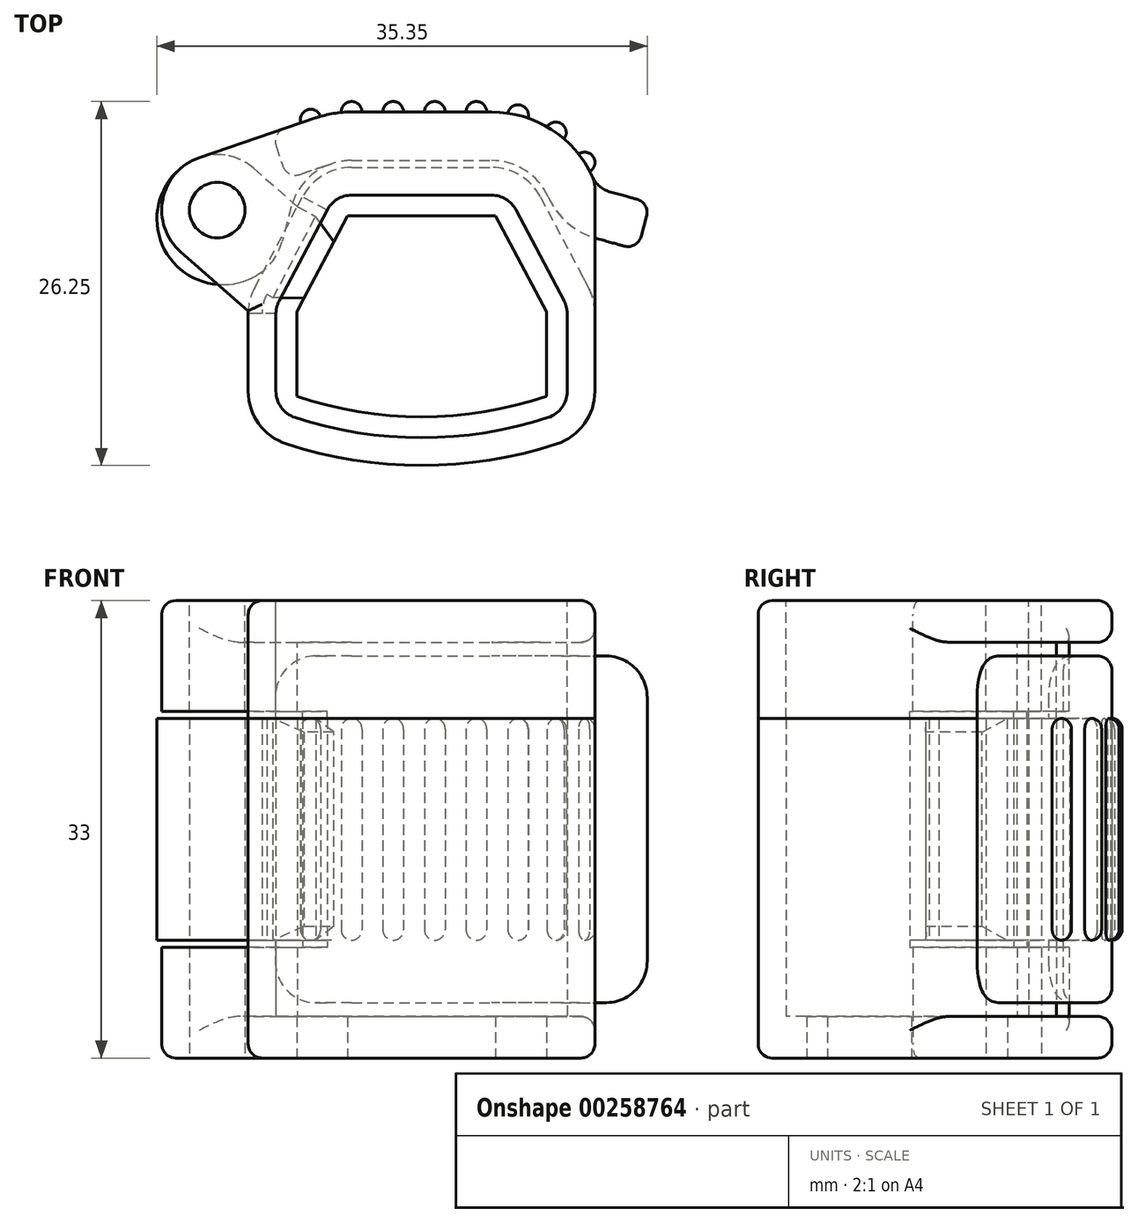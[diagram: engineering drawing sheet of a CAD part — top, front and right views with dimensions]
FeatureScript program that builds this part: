
annotation { "Feature Type Name" : "Feature", "Feature Type Description" : "" }
export const myFeature = defineFeature(function(context is Context, id is Id, definition is map)
    precondition{}
    {
        {
            var Q0;
            Q0=qCreatedBy(makeId("Top.planeOp"),FACE);
            var sketch = newSketch(context, id + "F0", { "sketchPlane" : qUnion([Q0])});
            skArc(sketch, "E0", {"start": v(-9.12, -27.9) * mm, "mid": v(0, -29.35) * mm, "end": v(9.12, -27.9) * mm});
            skLineSegment(sketch, "E1", {"start": v(-10.5, -26) * mm, "end": v(-10.5, -20.4) * mm});
            skLineSegment(sketch, "E2", {"start": v(-10.27, -19.47) * mm, "end": v(-6.81, -12.92) * mm});
            skLineSegment(sketch, "E3", {"start": v(-5.04, -11.85) * mm, "end": v(0, -11.85) * mm});
            skLineSegment(sketch, "E4", {"start": v(6.81, -12.92) * mm, "end": v(10.27, -19.47) * mm});
            skLineSegment(sketch, "E5", {"start": v(10.5, -20.4) * mm, "end": v(10.5, -26) * mm});
            skLineSegment(sketch, "E6", {"start": v(0, 0) * mm, "end": v(0, -29.35) * mm, "construction": true});
            skLineSegment(sketch, "E7", {"start": v(0, -11.85) * mm, "end": v(5.04, -11.85) * mm});
            skLineSegment(sketch, "E8", {"start": v(-6.25, -11.85) * mm, "end": v(0, 0) * mm, "construction": true});
            skLineSegment(sketch, "E9", {"start": v(6.25, -11.85) * mm, "end": v(0, 0) * mm, "construction": true});
            skPoint(sketch, "E10.visualSharp", {"position": v(-6.25, -11.85) * mm});
            skArc(sketch, "E10.filletArc", {"start": v(-5.04, -11.85) * mm, "mid": v(-6.08, -12.14) * mm, "end": v(-6.81, -12.92) * mm});
            skPoint(sketch, "E11.visualSharp", {"position": v(6.25, -11.85) * mm});
            skArc(sketch, "E11.filletArc", {"start": v(6.81, -12.92) * mm, "mid": v(6.08, -12.14) * mm, "end": v(5.04, -11.85) * mm});
            skPoint(sketch, "E12.visualSharp", {"position": v(10.5, -19.9) * mm});
            skArc(sketch, "E12.filletArc", {"start": v(10.5, -20.4) * mm, "mid": v(10.44, -19.92) * mm, "end": v(10.27, -19.47) * mm});
            skPoint(sketch, "E13.visualSharp", {"position": v(10.5, -27.4) * mm});
            skArc(sketch, "E13.filletArc", {"start": v(9.12, -27.9) * mm, "mid": v(10.12, -27.17) * mm, "end": v(10.5, -26) * mm});
            skPoint(sketch, "E14.visualSharp", {"position": v(-10.5, -27.4) * mm});
            skArc(sketch, "E14.filletArc", {"start": v(-10.5, -26) * mm, "mid": v(-10.12, -27.17) * mm, "end": v(-9.12, -27.9) * mm});
            skPoint(sketch, "E15.visualSharp", {"position": v(-10.5, -19.9) * mm});
            skArc(sketch, "E15.filletArc", {"start": v(-10.27, -19.47) * mm, "mid": v(-10.44, -19.92) * mm, "end": v(-10.5, -20.4) * mm});
            skSolve(sketch);
        }
        {
            var Q0;
            Q0=makeQuery(id+"F0.imprint","IMPRINT",FACE,{"disambiguationData":[TD([[makeQuery(id+"F0.imprint","IMPRINT",EDGE,{"derivedFrom":sQuery(id+"F0.wireOp",EDGE,"E0")}),1.0]])]});
            var sketch = newSketch(context, id + "F1", { "sketchPlane" : qUnion([Q0])});
            skLineSegment(sketch, "E16.0", {"start": v(-10.27, -19.47) * mm, "end": v(-7.19, -13.62) * mm, "construction": true});
            skLineSegment(sketch, "E17.0", {"start": v(6.81, -12.92) * mm, "end": v(10.27, -19.47) * mm});
            skLineSegment(sketch, "E18.0", {"start": v(0, -11.85) * mm, "end": v(5.04, -11.85) * mm});
            skLineSegment(sketch, "E19.0", {"start": v(-5.04, -11.85) * mm, "end": v(0, -11.85) * mm});
            skArc(sketch, "E20.0", {"start": v(-5.04, -11.85) * mm, "mid": v(-6.08, -12.14) * mm, "end": v(-6.81, -12.92) * mm});
            skArc(sketch, "E21.0", {"start": v(6.81, -12.92) * mm, "mid": v(6.08, -12.14) * mm, "end": v(5.04, -11.85) * mm});
            skLineSegment(sketch, "E22.0", {"start": v(-10.5, -26) * mm, "end": v(-10.5, -20.4) * mm});
            skArc(sketch, "E23.0", {"start": v(-10.5, -26) * mm, "mid": v(-10.12, -27.17) * mm, "end": v(-9.12, -27.9) * mm});
            skArc(sketch, "E24.0", {"start": v(-9.12, -27.9) * mm, "mid": v(0, -29.35) * mm, "end": v(9.12, -27.9) * mm});
            skArc(sketch, "E25.0", {"start": v(9.12, -27.9) * mm, "mid": v(10.12, -27.17) * mm, "end": v(10.5, -26) * mm});
            skLineSegment(sketch, "E26.0", {"start": v(10.5, -20.4) * mm, "end": v(10.5, -26) * mm});
            skArc(sketch, "E27.0", {"start": v(10.5, -20.4) * mm, "mid": v(10.44, -19.92) * mm, "end": v(10.27, -19.47) * mm});
            skArc(sketch, "E28.0", {"start": v(-10.27, -19.47) * mm, "mid": v(-10.44, -19.92) * mm, "end": v(-10.5, -20.4) * mm, "construction": true});
            skArc(sketch, "E29.0", {"start": v(-12.04, -18.54) * mm, "mid": v(-12.38, -19.44) * mm, "end": v(-12.5, -20.4) * mm});
            skLineSegment(sketch, "E29.1", {"start": v(-12.5, -26) * mm, "end": v(-12.5, -20.4) * mm});
            skArc(sketch, "E29.2", {"start": v(8.58, -11.98) * mm, "mid": v(7.1, -10.42) * mm, "end": v(5.04, -9.85) * mm});
            skLineSegment(sketch, "E29.3", {"start": v(0, -9.85) * mm, "end": v(5.04, -9.85) * mm});
            skLineSegment(sketch, "E29.4", {"start": v(-5.04, -9.85) * mm, "end": v(0, -9.85) * mm});
            skArc(sketch, "E29.5", {"start": v(-5.04, -9.85) * mm, "mid": v(-7.1, -10.42) * mm, "end": v(-8.58, -11.98) * mm});
            skLineSegment(sketch, "E29.6", {"start": v(8.58, -11.98) * mm, "end": v(12.04, -18.54) * mm});
            skArc(sketch, "E29.7", {"start": v(12.5, -20.4) * mm, "mid": v(12.38, -19.44) * mm, "end": v(12.04, -18.54) * mm});
            skLineSegment(sketch, "E29.8", {"start": v(-12.04, -18.54) * mm, "end": v(-8.95, -12.7) * mm});
            skLineSegment(sketch, "E29.9", {"start": v(12.5, -20.4) * mm, "end": v(12.5, -26) * mm});
            skArc(sketch, "E29.10", {"start": v(9.74, -29.8) * mm, "mid": v(11.74, -28.34) * mm, "end": v(12.5, -26) * mm});
            skArc(sketch, "E29.11", {"start": v(-9.74, -29.8) * mm, "mid": v(0, -31.35) * mm, "end": v(9.74, -29.8) * mm});
            skArc(sketch, "E29.12", {"start": v(-12.5, -26) * mm, "mid": v(-11.74, -28.34) * mm, "end": v(-9.74, -29.8) * mm});
            skArc(sketch, "E30.0", {"start": v(-11.15, -19) * mm, "mid": v(-11.41, -19.68) * mm, "end": v(-11.5, -20.4) * mm});
            skLineSegment(sketch, "E31", {"start": v(-10.5, -20.4) * mm, "end": v(-11.5, -20.4) * mm});
            skLineSegment(sketch, "E32", {"start": v(-11.15, -19) * mm, "end": v(-10.27, -19.47) * mm});
            skLineSegment(sketch, "E33", {"start": v(-6.81, -12.92) * mm, "end": v(-8.58, -11.98) * mm});
            skLineSegment(sketch, "E34.0", {"start": v(-7.19, -13.62) * mm, "end": v(-8.95, -12.7) * mm});
            skLineSegment(sketch, "E35", {"start": v(-7.19, -13.62) * mm, "end": v(-6.81, -12.92) * mm, "construction": true});
            skLineSegment(sketch, "E36", {"start": v(-11.15, -19) * mm, "end": v(-12.04, -18.54) * mm, "construction": true});
            skLineSegment(sketch, "E37", {"start": v(-11.5, -20.4) * mm, "end": v(-12.5, -20.4) * mm, "construction": true});
            skLineSegment(sketch, "E38.0", {"start": v(-8.94, -20.17) * mm, "end": v(-5.86, -14.32) * mm});
            skLineSegment(sketch, "E39", {"start": v(-7.19, -13.62) * mm, "end": v(-5.86, -14.32) * mm});
            skLineSegment(sketch, "E40", {"start": v(-10.27, -19.47) * mm, "end": v(-8.94, -20.17) * mm});
            skSolve(sketch);
        }
        {
            var Q0;
            Q0=makeQuery(id+"F0.imprint","IMPRINT",FACE,{"disambiguationData":[TD([[makeQuery(id+"F0.imprint","IMPRINT",EDGE,{"derivedFrom":sQuery(id+"F0.wireOp",EDGE,"E0")}),1.0]])]});
            var sketch = newSketch(context, id + "F2", { "sketchPlane" : qUnion([Q0])});
            skLineSegment(sketch, "E41.0", {"start": v(-10.27, -19.47) * mm, "end": v(-8.54, -16.2) * mm});
            skArc(sketch, "E42.0", {"start": v(-5.04, -11.85) * mm, "mid": v(-6.08, -12.14) * mm, "end": v(-6.81, -12.92) * mm});
            skLineSegment(sketch, "E43.0", {"start": v(-5.04, -11.85) * mm, "end": v(0, -11.85) * mm});
            skLineSegment(sketch, "E44.0", {"start": v(0, -11.85) * mm, "end": v(5.04, -11.85) * mm});
            skArc(sketch, "E45.0", {"start": v(6.81, -12.92) * mm, "mid": v(6.08, -12.14) * mm, "end": v(5.04, -11.85) * mm});
            skLineSegment(sketch, "E46.0", {"start": v(6.81, -12.92) * mm, "end": v(10.27, -19.47) * mm});
            skArc(sketch, "E47.0", {"start": v(10.5, -20.4) * mm, "mid": v(10.44, -19.92) * mm, "end": v(10.27, -19.47) * mm});
            skLineSegment(sketch, "E48.0", {"start": v(10.5, -20.4) * mm, "end": v(10.5, -26) * mm});
            skArc(sketch, "E49.0", {"start": v(9.12, -27.9) * mm, "mid": v(10.12, -27.17) * mm, "end": v(10.5, -26) * mm});
            skArc(sketch, "E50.0", {"start": v(-9.12, -27.9) * mm, "mid": v(0, -29.35) * mm, "end": v(9.12, -27.9) * mm});
            skArc(sketch, "E51.0", {"start": v(-10.5, -26) * mm, "mid": v(-10.12, -27.17) * mm, "end": v(-9.12, -27.9) * mm});
            skLineSegment(sketch, "E52.0", {"start": v(-10.5, -26) * mm, "end": v(-10.5, -20.4) * mm});
            skArc(sketch, "E53.0", {"start": v(-10.27, -19.47) * mm, "mid": v(-10.44, -19.92) * mm, "end": v(-10.5, -20.4) * mm});
            skArc(sketch, "E54.0", {"start": v(-5.04, -5.85) * mm, "mid": v(-6.35, -5.96) * mm, "end": v(-7.63, -6.28) * mm});
            skLineSegment(sketch, "E54.1", {"start": v(-5.04, -5.85) * mm, "end": v(0, -5.85) * mm});
            skLineSegment(sketch, "E54.2", {"start": v(0, -5.85) * mm, "end": v(5.04, -5.85) * mm});
            skArc(sketch, "E54.3", {"start": v(12.32, -10.52) * mm, "mid": v(9.37, -7.12) * mm, "end": v(5.04, -5.85) * mm});
            skLineSegment(sketch, "E55.0", {"start": v(-12.5, -26) * mm, "end": v(-12.5, -20.2) * mm});
            skLineSegment(sketch, "E55.1", {"start": v(12.5, -20.4) * mm, "end": v(12.5, -26) * mm});
            skArc(sketch, "E55.2", {"start": v(9.74, -29.8) * mm, "mid": v(11.74, -28.34) * mm, "end": v(12.5, -26) * mm});
            skArc(sketch, "E55.3", {"start": v(-9.74, -29.8) * mm, "mid": v(0, -31.35) * mm, "end": v(9.74, -29.8) * mm});
            skArc(sketch, "E55.4", {"start": v(-12.5, -26) * mm, "mid": v(-11.74, -28.34) * mm, "end": v(-9.74, -29.8) * mm});
            skLineSegment(sketch, "E56", {"start": v(12.5, -20.4) * mm, "end": v(12.5, -11.35) * mm});
            skPoint(sketch, "E57.visualSharp", {"position": v(12.5, -10.95) * mm});
            skArc(sketch, "E57.filletArc", {"start": v(12.5, -11.35) * mm, "mid": v(12.45, -10.93) * mm, "end": v(12.32, -10.52) * mm});
            skLineSegment(sketch, "E58", {"start": v(-8.54, -16.2) * mm, "end": v(-6.81, -12.92) * mm});
            skLineSegment(sketch, "E59", {"start": v(-8.54, -16.2) * mm, "end": v(-14.73, -12.93) * mm, "construction": true});
            skCircle(sketch, "E60", {"center": v(-14.73, -12.93) * mm, "radius": 2 * mm});
            skLineSegment(sketch, "E61", {"start": v(-16.02, -9.14) * mm, "end": v(-7.63, -6.28) * mm});
            skLineSegment(sketch, "E62", {"start": v(-17.37, -15.94) * mm, "end": v(-12.5, -20.2) * mm});
            skArc(sketch, "E63", {"start": v(-16.02, -9.14) * mm, "mid": v(-18.66, -12.15) * mm, "end": v(-17.37, -15.94) * mm});
            skArc(sketch, "E64", {"start": v(-17.37, -15.94) * mm, "mid": v(-10.8, -13.7) * mm, "end": v(-16.02, -9.14) * mm, "construction": true});
            skSolve(sketch);
        }
        {
            var Q0;
            Q0 = qSketchRegion(id + "F2", true);
            extrude(context, id + "F3", {"entities" : qUnion([Q0]), "depth" : 3 * mm});
        }
        {
            var Q0;
            Q0=makeQuery(id+"F3.opExtrude","CAP_FACE",FACE,{"disambiguationData":[OSD([sQuery(id+"F2.wireOp",EDGE,"E41.0"),sQuery(id+"F2.wireOp",EDGE,"E42.0"),sQuery(id+"F2.wireOp",EDGE,"E43.0"),sQuery(id+"F2.wireOp",EDGE,"E44.0"),sQuery(id+"F2.wireOp",EDGE,"E45.0"),sQuery(id+"F2.wireOp",EDGE,"E46.0"),sQuery(id+"F2.wireOp",EDGE,"E47.0"),sQuery(id+"F2.wireOp",EDGE,"E48.0"),sQuery(id+"F2.wireOp",EDGE,"E49.0"),sQuery(id+"F2.wireOp",EDGE,"E50.0"),sQuery(id+"F2.wireOp",EDGE,"E51.0"),sQuery(id+"F2.wireOp",EDGE,"E52.0"),sQuery(id+"F2.wireOp",EDGE,"E53.0"),sQuery(id+"F2.wireOp",EDGE,"E54.0"),sQuery(id+"F2.wireOp",EDGE,"E54.1"),sQuery(id+"F2.wireOp",EDGE,"E54.2"),sQuery(id+"F2.wireOp",EDGE,"E54.3"),sQuery(id+"F2.wireOp",EDGE,"E55.0"),sQuery(id+"F2.wireOp",EDGE,"E55.1"),sQuery(id+"F2.wireOp",EDGE,"E55.2"),sQuery(id+"F2.wireOp",EDGE,"E55.3"),sQuery(id+"F2.wireOp",EDGE,"E55.4"),sQuery(id+"F2.wireOp",EDGE,"E56"),sQuery(id+"F2.wireOp",EDGE,"E57.filletArc"),sQuery(id+"F2.wireOp",EDGE,"E58"),sQuery(id+"F2.wireOp",EDGE,"E60"),sQuery(id+"F2.wireOp",EDGE,"E61"),sQuery(id+"F2.wireOp",EDGE,"E62"),sQuery(id+"F2.wireOp",EDGE,"E63")])],"isStart":false});
            var sketch = newSketch(context, id + "F4", { "sketchPlane" : qUnion([Q0])});
            skLineSegment(sketch, "E65.0", {"start": v(-17.37, -15.94) * mm, "end": v(-17.37, -15.94) * mm});
            skCircle(sketch, "E66.0", {"center": v(-14.73, -12.93) * mm, "radius": 2 * mm});
            skArc(sketch, "E67.0", {"start": v(-16.02, -9.14) * mm, "mid": v(-18.66, -12.15) * mm, "end": v(-17.37, -15.94) * mm});
            skLineSegment(sketch, "E68.0", {"start": v(-17.37, -15.94) * mm, "end": v(-12.5, -20.2) * mm});
            skLineSegment(sketch, "E69.0", {"start": v(-12.5, -26) * mm, "end": v(-12.5, -20.2) * mm});
            skArc(sketch, "E70.0", {"start": v(-12.5, -26) * mm, "mid": v(-11.74, -28.34) * mm, "end": v(-9.74, -29.8) * mm});
            skArc(sketch, "E71.0", {"start": v(-9.74, -29.8) * mm, "mid": v(0, -31.35) * mm, "end": v(9.74, -29.8) * mm});
            skArc(sketch, "E72.0", {"start": v(9.74, -29.8) * mm, "mid": v(11.74, -28.34) * mm, "end": v(12.5, -26) * mm});
            skArc(sketch, "E73.0", {"start": v(9.12, -27.9) * mm, "mid": v(10.12, -27.17) * mm, "end": v(10.5, -26) * mm});
            skArc(sketch, "E74.0", {"start": v(-9.12, -27.9) * mm, "mid": v(0, -29.35) * mm, "end": v(9.12, -27.9) * mm});
            skArc(sketch, "E75.0", {"start": v(-10.5, -26) * mm, "mid": v(-10.12, -27.17) * mm, "end": v(-9.12, -27.9) * mm});
            skLineSegment(sketch, "E76.0", {"start": v(-10.5, -26) * mm, "end": v(-10.5, -20.4) * mm});
            skArc(sketch, "E77.0", {"start": v(-10.27, -19.47) * mm, "mid": v(-10.44, -19.92) * mm, "end": v(-10.5, -20.4) * mm});
            skLineSegment(sketch, "E78.0", {"start": v(-10.27, -19.47) * mm, "end": v(-8.54, -16.2) * mm});
            skLineSegment(sketch, "E79.0", {"start": v(-8.54, -16.2) * mm, "end": v(-6.81, -12.92) * mm});
            skArc(sketch, "E80.0", {"start": v(-5.04, -11.85) * mm, "mid": v(-6.08, -12.14) * mm, "end": v(-6.81, -12.92) * mm});
            skLineSegment(sketch, "E81.0", {"start": v(-5.04, -11.85) * mm, "end": v(0, -11.85) * mm});
            skLineSegment(sketch, "E82.0", {"start": v(0, -11.85) * mm, "end": v(5.04, -11.85) * mm});
            skArc(sketch, "E83.0", {"start": v(6.81, -12.92) * mm, "mid": v(6.08, -12.14) * mm, "end": v(5.04, -11.85) * mm});
            skLineSegment(sketch, "E84.0", {"start": v(6.81, -12.92) * mm, "end": v(10.27, -19.47) * mm});
            skArc(sketch, "E85.0", {"start": v(10.5, -20.4) * mm, "mid": v(10.44, -19.92) * mm, "end": v(10.27, -19.47) * mm});
            skLineSegment(sketch, "E86.0", {"start": v(10.5, -20.4) * mm, "end": v(10.5, -26) * mm});
            skLineSegment(sketch, "E87.0", {"start": v(12.5, -20.4) * mm, "end": v(12.5, -26) * mm});
            skArc(sketch, "E88.0", {"start": v(12.5, -20.4) * mm, "mid": v(12.38, -19.44) * mm, "end": v(12.04, -18.54) * mm});
            skLineSegment(sketch, "E89.0", {"start": v(8.58, -11.98) * mm, "end": v(12.04, -18.54) * mm});
            skArc(sketch, "E90.0", {"start": v(8.58, -11.98) * mm, "mid": v(7.1, -10.42) * mm, "end": v(5.04, -9.85) * mm});
            skLineSegment(sketch, "E91.0", {"start": v(0, -9.85) * mm, "end": v(5.04, -9.85) * mm});
            skLineSegment(sketch, "E92.0", {"start": v(-5.04, -9.85) * mm, "end": v(0, -9.85) * mm});
            skLineSegment(sketch, "E93.0", {"start": v(-8.54, -16.2) * mm, "end": v(-14.73, -12.93) * mm, "construction": true});
            skArc(sketch, "E94.0", {"start": v(-5.04, -9.85) * mm, "mid": v(-7.1, -10.42) * mm, "end": v(-8.58, -11.98) * mm});
            skLineSegment(sketch, "E95", {"start": v(-8.95, -12.67) * mm, "end": v(-8.58, -11.98) * mm});
            skLineSegment(sketch, "E96", {"start": v(-17.37, -15.94) * mm, "end": v(-12.78, -19.95) * mm});
            skArc(sketch, "E97", {"start": v(-17.37, -15.94) * mm, "mid": v(-11.72, -15.56) * mm, "end": v(-12.1, -9.92) * mm, "construction": true});
            skLineSegment(sketch, "E98", {"start": v(-12.1, -9.92) * mm, "end": v(-8.95, -12.67) * mm});
            skArc(sketch, "E99", {"start": v(-12.1, -9.92) * mm, "mid": v(-13.96, -9) * mm, "end": v(-16.02, -9.14) * mm});
            skLineSegment(sketch, "E100", {"start": v(-12.78, -19.95) * mm, "end": v(-8.95, -12.67) * mm, "construction": true});
            skSolve(sketch);
        }
        {
            var Q0;
            Q0 = qSketchRegion(id + "F4", true);
            extrude(context, id + "F5", {"entities" : qUnion([Q0]), "operationType" : NewBodyOperationType.ADD, "depth" : 5 * mm});
        }
        {
            var Q0;
            Q0=makeQuery(id+"F5.opExtrude","CAP_FACE",FACE,{"disambiguationData":[OSD([sQuery(id+"F4.wireOp",EDGE,"E66.0"),sQuery(id+"F4.wireOp",EDGE,"E67.0"),sQuery(id+"F4.wireOp",EDGE,"E68.0"),sQuery(id+"F4.wireOp",EDGE,"E69.0"),sQuery(id+"F4.wireOp",EDGE,"E70.0"),sQuery(id+"F4.wireOp",EDGE,"E71.0"),sQuery(id+"F4.wireOp",EDGE,"E72.0"),sQuery(id+"F4.wireOp",EDGE,"E73.0"),sQuery(id+"F4.wireOp",EDGE,"E74.0"),sQuery(id+"F4.wireOp",EDGE,"E75.0"),sQuery(id+"F4.wireOp",EDGE,"E76.0"),sQuery(id+"F4.wireOp",EDGE,"E77.0"),sQuery(id+"F4.wireOp",EDGE,"E78.0"),sQuery(id+"F4.wireOp",EDGE,"E79.0"),sQuery(id+"F4.wireOp",EDGE,"E80.0"),sQuery(id+"F4.wireOp",EDGE,"E81.0"),sQuery(id+"F4.wireOp",EDGE,"E82.0"),sQuery(id+"F4.wireOp",EDGE,"E83.0"),sQuery(id+"F4.wireOp",EDGE,"E84.0"),sQuery(id+"F4.wireOp",EDGE,"E85.0"),sQuery(id+"F4.wireOp",EDGE,"E86.0"),sQuery(id+"F4.wireOp",EDGE,"E87.0"),sQuery(id+"F4.wireOp",EDGE,"E88.0"),sQuery(id+"F4.wireOp",EDGE,"E89.0"),sQuery(id+"F4.wireOp",EDGE,"E90.0"),sQuery(id+"F4.wireOp",EDGE,"E91.0"),sQuery(id+"F4.wireOp",EDGE,"E92.0"),sQuery(id+"F4.wireOp",EDGE,"E94.0"),sQuery(id+"F4.wireOp",EDGE,"E95"),sQuery(id+"F4.wireOp",EDGE,"E96"),sQuery(id+"F4.wireOp",EDGE,"E98"),sQuery(id+"F4.wireOp",EDGE,"E99")])],"isStart":false});
            var sketch = newSketch(context, id + "F6", { "sketchPlane" : qUnion([Q0])});
            skLineSegment(sketch, "E101.0", {"start": v(-12.5, -26) * mm, "end": v(-12.5, -20.4) * mm});
            skLineSegment(sketch, "E102.0", {"start": v(-10.5, -26) * mm, "end": v(-10.5, -20.4) * mm});
            skArc(sketch, "E103.0", {"start": v(-10.5, -26) * mm, "mid": v(-10.12, -27.17) * mm, "end": v(-9.12, -27.9) * mm});
            skLineSegment(sketch, "E104.0", {"start": v(-10.5, -20.4) * mm, "end": v(-11.5, -20.4) * mm});
            skLineSegment(sketch, "E105.0", {"start": v(-11.5, -20.4) * mm, "end": v(-12.5, -20.4) * mm});
            skArc(sketch, "E106.0", {"start": v(-12.5, -26) * mm, "mid": v(-11.74, -28.34) * mm, "end": v(-9.74, -29.8) * mm});
            skArc(sketch, "E107.0", {"start": v(-9.74, -29.8) * mm, "mid": v(0, -31.35) * mm, "end": v(9.74, -29.8) * mm});
            skArc(sketch, "E108.0", {"start": v(-9.12, -27.9) * mm, "mid": v(0, -29.35) * mm, "end": v(9.12, -27.9) * mm});
            skArc(sketch, "E109.0", {"start": v(9.12, -27.9) * mm, "mid": v(10.12, -27.17) * mm, "end": v(10.5, -26) * mm});
            skArc(sketch, "E110.0", {"start": v(9.74, -29.8) * mm, "mid": v(11.74, -28.34) * mm, "end": v(12.5, -26) * mm});
            skLineSegment(sketch, "E111.0", {"start": v(12.5, -20.4) * mm, "end": v(12.5, -26) * mm});
            skLineSegment(sketch, "E112.0", {"start": v(10.5, -20.4) * mm, "end": v(10.5, -26) * mm});
            skArc(sketch, "E113.0", {"start": v(10.5, -20.4) * mm, "mid": v(10.44, -19.92) * mm, "end": v(10.27, -19.47) * mm});
            skArc(sketch, "E114.0", {"start": v(12.5, -20.4) * mm, "mid": v(12.38, -19.44) * mm, "end": v(12.04, -18.54) * mm});
            skLineSegment(sketch, "E115.0", {"start": v(8.58, -11.98) * mm, "end": v(12.04, -18.54) * mm});
            skLineSegment(sketch, "E116.0", {"start": v(6.81, -12.92) * mm, "end": v(10.27, -19.47) * mm});
            skArc(sketch, "E117.0", {"start": v(6.81, -12.92) * mm, "mid": v(6.08, -12.14) * mm, "end": v(5.04, -11.85) * mm});
            skArc(sketch, "E118.0", {"start": v(8.58, -11.98) * mm, "mid": v(7.1, -10.42) * mm, "end": v(5.04, -9.85) * mm});
            skLineSegment(sketch, "E119.0", {"start": v(0, -9.85) * mm, "end": v(5.04, -9.85) * mm});
            skLineSegment(sketch, "E120.0", {"start": v(0, -11.85) * mm, "end": v(5.04, -11.85) * mm});
            skLineSegment(sketch, "E121.0", {"start": v(-5.04, -9.85) * mm, "end": v(0, -9.85) * mm});
            skLineSegment(sketch, "E122.0", {"start": v(-5.04, -11.85) * mm, "end": v(0, -11.85) * mm});
            skArc(sketch, "E123.0", {"start": v(-5.04, -11.85) * mm, "mid": v(-6.08, -12.14) * mm, "end": v(-6.81, -12.92) * mm});
            skArc(sketch, "E124.0", {"start": v(-5.04, -9.85) * mm, "mid": v(-7.1, -10.42) * mm, "end": v(-8.58, -11.98) * mm});
            skLineSegment(sketch, "E125.0", {"start": v(-6.81, -12.92) * mm, "end": v(-8.58, -11.98) * mm});
            skSolve(sketch);
        }
        {
            var Q0;
            Q0 = qSketchRegion(id + "F6", true);
            extrude(context, id + "F7", {"entities" : qUnion([Q0]), "operationType" : NewBodyOperationType.ADD, "depth" : 0.5 * mm});
        }
        {
            var Q0;
            Q0=makeQuery(id+"F0.imprint","IMPRINT",FACE,{"disambiguationData":[TD([[makeQuery(id+"F0.imprint","IMPRINT",EDGE,{"derivedFrom":sQuery(id+"F0.wireOp",EDGE,"E0")}),1.0]])]});
            var sketch = newSketch(context, id + "F8", { "sketchPlane" : qUnion([Q0])});
            skLineSegment(sketch, "E126.0.0", {"start": v(-12.5, -20.2) * mm, "end": v(-12.5, -26) * mm});
            skArc(sketch, "E126.0.1", {"start": v(-12.5, -26) * mm, "mid": v(-11.74, -28.34) * mm, "end": v(-9.74, -29.8) * mm});
            skArc(sketch, "E126.0.2", {"start": v(-9.74, -29.8) * mm, "mid": v(0, -31.35) * mm, "end": v(9.74, -29.8) * mm});
            skArc(sketch, "E126.0.3", {"start": v(9.74, -29.8) * mm, "mid": v(11.74, -28.34) * mm, "end": v(12.5, -26) * mm});
            skLineSegment(sketch, "E126.0.4", {"start": v(12.5, -26) * mm, "end": v(12.5, -20.4) * mm});
            skLineSegment(sketch, "E126.0.5", {"start": v(12.5, -20.4) * mm, "end": v(12.5, -11.35) * mm});
            skArc(sketch, "E126.0.6", {"start": v(12.5, -11.35) * mm, "mid": v(12.45, -10.93) * mm, "end": v(12.32, -10.52) * mm});
            skArc(sketch, "E126.0.7", {"start": v(12.32, -10.52) * mm, "mid": v(9.37, -7.12) * mm, "end": v(5.04, -5.85) * mm});
            skLineSegment(sketch, "E126.0.8", {"start": v(5.04, -5.85) * mm, "end": v(0, -5.85) * mm});
            skLineSegment(sketch, "E126.0.9", {"start": v(0, -5.85) * mm, "end": v(-5.04, -5.85) * mm});
            skArc(sketch, "E126.0.10", {"start": v(-5.04, -5.85) * mm, "mid": v(-6.35, -5.96) * mm, "end": v(-7.63, -6.28) * mm});
            skLineSegment(sketch, "E126.0.11", {"start": v(-7.63, -6.28) * mm, "end": v(-16.02, -9.14) * mm});
            skArc(sketch, "E126.0.12", {"start": v(-16.02, -9.14) * mm, "mid": v(-18.66, -12.15) * mm, "end": v(-17.37, -15.94) * mm});
            skLineSegment(sketch, "E126.0.13", {"start": v(-17.37, -15.94) * mm, "end": v(-12.5, -20.2) * mm});
            skCircle(sketch, "E127.0", {"center": v(-14.73, -12.93) * mm, "radius": 2 * mm});
            skLineSegment(sketch, "E128.0.0", {"start": v(5.04, -11.85) * mm, "end": v(0, -11.85) * mm, "construction": true});
            skLineSegment(sketch, "E128.0.1", {"start": v(0, -11.85) * mm, "end": v(-5.04, -11.85) * mm, "construction": true});
            skArc(sketch, "E128.0.2", {"start": v(-5.04, -11.85) * mm, "mid": v(-6.08, -12.14) * mm, "end": v(-6.81, -12.92) * mm, "construction": true});
            skLineSegment(sketch, "E128.0.3", {"start": v(-6.81, -12.92) * mm, "end": v(-8.54, -16.2) * mm, "construction": true});
            skLineSegment(sketch, "E128.0.4", {"start": v(-8.54, -16.2) * mm, "end": v(-10.27, -19.47) * mm, "construction": true});
            skArc(sketch, "E128.0.5", {"start": v(-10.27, -19.47) * mm, "mid": v(-10.44, -19.92) * mm, "end": v(-10.5, -20.4) * mm, "construction": true});
            skLineSegment(sketch, "E128.0.6", {"start": v(-10.5, -20.4) * mm, "end": v(-10.5, -26) * mm, "construction": true});
            skArc(sketch, "E128.0.7", {"start": v(-10.5, -26) * mm, "mid": v(-10.12, -27.17) * mm, "end": v(-9.12, -27.9) * mm, "construction": true});
            skArc(sketch, "E128.0.8", {"start": v(-9.12, -27.9) * mm, "mid": v(0, -29.35) * mm, "end": v(9.12, -27.9) * mm, "construction": true});
            skArc(sketch, "E128.0.9", {"start": v(9.12, -27.9) * mm, "mid": v(10.12, -27.17) * mm, "end": v(10.5, -26) * mm, "construction": true});
            skLineSegment(sketch, "E128.0.10", {"start": v(10.5, -26) * mm, "end": v(10.5, -20.4) * mm, "construction": true});
            skArc(sketch, "E128.0.11", {"start": v(10.5, -20.4) * mm, "mid": v(10.44, -19.92) * mm, "end": v(10.27, -19.47) * mm, "construction": true});
            skLineSegment(sketch, "E128.0.12", {"start": v(10.27, -19.47) * mm, "end": v(6.81, -12.92) * mm, "construction": true});
            skArc(sketch, "E128.0.13", {"start": v(6.81, -12.92) * mm, "mid": v(6.08, -12.14) * mm, "end": v(5.04, -11.85) * mm, "construction": true});
            skLineSegment(sketch, "E129.0", {"start": v(9, -20.28) * mm, "end": v(5.35, -13.35) * mm});
            skLineSegment(sketch, "E129.1", {"start": v(9, -26.35) * mm, "end": v(9, -20.28) * mm});
            skLineSegment(sketch, "E129.2", {"start": v(5.35, -13.35) * mm, "end": v(0, -13.35) * mm});
            skArc(sketch, "E129.3", {"start": v(-9, -26.35) * mm, "mid": v(0, -27.85) * mm, "end": v(9, -26.35) * mm});
            skLineSegment(sketch, "E129.4", {"start": v(0, -13.35) * mm, "end": v(-5.35, -13.35) * mm});
            skLineSegment(sketch, "E129.5", {"start": v(-5.35, -13.35) * mm, "end": v(-7.21, -16.9) * mm});
            skLineSegment(sketch, "E129.6", {"start": v(-7.21, -16.9) * mm, "end": v(-9, -20.28) * mm});
            skLineSegment(sketch, "E129.7", {"start": v(-9, -20.28) * mm, "end": v(-9, -26.35) * mm});
            skSolve(sketch);
        }
        {
            var Q0;
            Q0=makeQuery(id+"F3.opExtrude","SWEPT_BODY",BODY,{"disambiguationData":[OSD([sQuery(id+"F2.wireOp",EDGE,"E41.0"),sQuery(id+"F2.wireOp",EDGE,"E42.0"),sQuery(id+"F2.wireOp",EDGE,"E43.0"),sQuery(id+"F2.wireOp",EDGE,"E44.0"),sQuery(id+"F2.wireOp",EDGE,"E45.0"),sQuery(id+"F2.wireOp",EDGE,"E46.0"),sQuery(id+"F2.wireOp",EDGE,"E47.0"),sQuery(id+"F2.wireOp",EDGE,"E48.0"),sQuery(id+"F2.wireOp",EDGE,"E49.0"),sQuery(id+"F2.wireOp",EDGE,"E50.0"),sQuery(id+"F2.wireOp",EDGE,"E51.0"),sQuery(id+"F2.wireOp",EDGE,"E52.0"),sQuery(id+"F2.wireOp",EDGE,"E53.0"),sQuery(id+"F2.wireOp",EDGE,"E54.0"),sQuery(id+"F2.wireOp",EDGE,"E54.1"),sQuery(id+"F2.wireOp",EDGE,"E54.2"),sQuery(id+"F2.wireOp",EDGE,"E54.3"),sQuery(id+"F2.wireOp",EDGE,"E55.0"),sQuery(id+"F2.wireOp",EDGE,"E55.1"),sQuery(id+"F2.wireOp",EDGE,"E55.2"),sQuery(id+"F2.wireOp",EDGE,"E55.3"),sQuery(id+"F2.wireOp",EDGE,"E55.4"),sQuery(id+"F2.wireOp",EDGE,"E56"),sQuery(id+"F2.wireOp",EDGE,"E57.filletArc"),sQuery(id+"F2.wireOp",EDGE,"E58"),sQuery(id+"F2.wireOp",EDGE,"E60"),sQuery(id+"F2.wireOp",EDGE,"E61"),sQuery(id+"F2.wireOp",EDGE,"E62"),sQuery(id+"F2.wireOp",EDGE,"E63")])]});
            var Q1;
            Q1=makeQuery(id+"F7.opExtrude","CAP_FACE",FACE,{"disambiguationData":[OSD([sQuery(id+"F6.wireOp",EDGE,"E101.0"),sQuery(id+"F6.wireOp",EDGE,"E102.0"),sQuery(id+"F6.wireOp",EDGE,"E103.0"),sQuery(id+"F6.wireOp",EDGE,"E104.0"),sQuery(id+"F6.wireOp",EDGE,"E105.0"),sQuery(id+"F6.wireOp",EDGE,"E106.0"),sQuery(id+"F6.wireOp",EDGE,"E107.0"),sQuery(id+"F6.wireOp",EDGE,"E108.0"),sQuery(id+"F6.wireOp",EDGE,"E109.0"),sQuery(id+"F6.wireOp",EDGE,"E110.0"),sQuery(id+"F6.wireOp",EDGE,"E111.0"),sQuery(id+"F6.wireOp",EDGE,"E112.0"),sQuery(id+"F6.wireOp",EDGE,"E113.0"),sQuery(id+"F6.wireOp",EDGE,"E114.0"),sQuery(id+"F6.wireOp",EDGE,"E115.0"),sQuery(id+"F6.wireOp",EDGE,"E116.0"),sQuery(id+"F6.wireOp",EDGE,"E117.0"),sQuery(id+"F6.wireOp",EDGE,"E118.0"),sQuery(id+"F6.wireOp",EDGE,"E119.0"),sQuery(id+"F6.wireOp",EDGE,"E120.0"),sQuery(id+"F6.wireOp",EDGE,"E121.0"),sQuery(id+"F6.wireOp",EDGE,"E122.0"),sQuery(id+"F6.wireOp",EDGE,"E123.0"),sQuery(id+"F6.wireOp",EDGE,"E124.0"),sQuery(id+"F6.wireOp",EDGE,"E125.0")])],"isStart":false});
            transform(context, id + "F9", {"entities" : qUnion([Q0]), "transformType" : TransformType.TRANSLATION_DISTANCE, "transformDirection" : qUnion([Q1]), "distance" : 33 * mm, "makeCopy" : false});
        }
        {
            var Q0;
            Q0=makeQuery(id+"F3.opExtrude","SWEPT_BODY",BODY,{"disambiguationData":[OSD([sQuery(id+"F2.wireOp",EDGE,"E41.0"),sQuery(id+"F2.wireOp",EDGE,"E42.0"),sQuery(id+"F2.wireOp",EDGE,"E43.0"),sQuery(id+"F2.wireOp",EDGE,"E44.0"),sQuery(id+"F2.wireOp",EDGE,"E45.0"),sQuery(id+"F2.wireOp",EDGE,"E46.0"),sQuery(id+"F2.wireOp",EDGE,"E47.0"),sQuery(id+"F2.wireOp",EDGE,"E48.0"),sQuery(id+"F2.wireOp",EDGE,"E49.0"),sQuery(id+"F2.wireOp",EDGE,"E50.0"),sQuery(id+"F2.wireOp",EDGE,"E51.0"),sQuery(id+"F2.wireOp",EDGE,"E52.0"),sQuery(id+"F2.wireOp",EDGE,"E53.0"),sQuery(id+"F2.wireOp",EDGE,"E54.0"),sQuery(id+"F2.wireOp",EDGE,"E54.1"),sQuery(id+"F2.wireOp",EDGE,"E54.2"),sQuery(id+"F2.wireOp",EDGE,"E54.3"),sQuery(id+"F2.wireOp",EDGE,"E55.0"),sQuery(id+"F2.wireOp",EDGE,"E55.1"),sQuery(id+"F2.wireOp",EDGE,"E55.2"),sQuery(id+"F2.wireOp",EDGE,"E55.3"),sQuery(id+"F2.wireOp",EDGE,"E55.4"),sQuery(id+"F2.wireOp",EDGE,"E56"),sQuery(id+"F2.wireOp",EDGE,"E57.filletArc"),sQuery(id+"F2.wireOp",EDGE,"E58"),sQuery(id+"F2.wireOp",EDGE,"E60"),sQuery(id+"F2.wireOp",EDGE,"E61"),sQuery(id+"F2.wireOp",EDGE,"E62"),sQuery(id+"F2.wireOp",EDGE,"E63")])]});
            var Q1;
            Q1=makeQuery(id+"F3.opExtrude","CAP_FACE",FACE,{"disambiguationData":[OSD([sQuery(id+"F2.wireOp",EDGE,"E41.0"),sQuery(id+"F2.wireOp",EDGE,"E42.0"),sQuery(id+"F2.wireOp",EDGE,"E43.0"),sQuery(id+"F2.wireOp",EDGE,"E44.0"),sQuery(id+"F2.wireOp",EDGE,"E45.0"),sQuery(id+"F2.wireOp",EDGE,"E46.0"),sQuery(id+"F2.wireOp",EDGE,"E47.0"),sQuery(id+"F2.wireOp",EDGE,"E48.0"),sQuery(id+"F2.wireOp",EDGE,"E49.0"),sQuery(id+"F2.wireOp",EDGE,"E50.0"),sQuery(id+"F2.wireOp",EDGE,"E51.0"),sQuery(id+"F2.wireOp",EDGE,"E52.0"),sQuery(id+"F2.wireOp",EDGE,"E53.0"),sQuery(id+"F2.wireOp",EDGE,"E54.0"),sQuery(id+"F2.wireOp",EDGE,"E54.1"),sQuery(id+"F2.wireOp",EDGE,"E54.2"),sQuery(id+"F2.wireOp",EDGE,"E54.3"),sQuery(id+"F2.wireOp",EDGE,"E55.0"),sQuery(id+"F2.wireOp",EDGE,"E55.1"),sQuery(id+"F2.wireOp",EDGE,"E55.2"),sQuery(id+"F2.wireOp",EDGE,"E55.3"),sQuery(id+"F2.wireOp",EDGE,"E55.4"),sQuery(id+"F2.wireOp",EDGE,"E56"),sQuery(id+"F2.wireOp",EDGE,"E57.filletArc"),sQuery(id+"F2.wireOp",EDGE,"E58"),sQuery(id+"F2.wireOp",EDGE,"E60"),sQuery(id+"F2.wireOp",EDGE,"E61"),sQuery(id+"F2.wireOp",EDGE,"E62"),sQuery(id+"F2.wireOp",EDGE,"E63")])],"isStart":true});
            mirror(context, id + "F10", {"entities" : qUnion([Q0]), "mirrorPlane" : qUnion([Q1])});
        }
        {
            var Q0;
            Q0=makeQuery(id+"F3.opExtrude","SWEPT_BODY",BODY,{"disambiguationData":[OSD([sQuery(id+"F2.wireOp",EDGE,"E41.0"),sQuery(id+"F2.wireOp",EDGE,"E42.0"),sQuery(id+"F2.wireOp",EDGE,"E43.0"),sQuery(id+"F2.wireOp",EDGE,"E44.0"),sQuery(id+"F2.wireOp",EDGE,"E45.0"),sQuery(id+"F2.wireOp",EDGE,"E46.0"),sQuery(id+"F2.wireOp",EDGE,"E47.0"),sQuery(id+"F2.wireOp",EDGE,"E48.0"),sQuery(id+"F2.wireOp",EDGE,"E49.0"),sQuery(id+"F2.wireOp",EDGE,"E50.0"),sQuery(id+"F2.wireOp",EDGE,"E51.0"),sQuery(id+"F2.wireOp",EDGE,"E52.0"),sQuery(id+"F2.wireOp",EDGE,"E53.0"),sQuery(id+"F2.wireOp",EDGE,"E54.0"),sQuery(id+"F2.wireOp",EDGE,"E54.1"),sQuery(id+"F2.wireOp",EDGE,"E54.2"),sQuery(id+"F2.wireOp",EDGE,"E54.3"),sQuery(id+"F2.wireOp",EDGE,"E55.0"),sQuery(id+"F2.wireOp",EDGE,"E55.1"),sQuery(id+"F2.wireOp",EDGE,"E55.2"),sQuery(id+"F2.wireOp",EDGE,"E55.3"),sQuery(id+"F2.wireOp",EDGE,"E55.4"),sQuery(id+"F2.wireOp",EDGE,"E56"),sQuery(id+"F2.wireOp",EDGE,"E57.filletArc"),sQuery(id+"F2.wireOp",EDGE,"E58"),sQuery(id+"F2.wireOp",EDGE,"E60"),sQuery(id+"F2.wireOp",EDGE,"E61"),sQuery(id+"F2.wireOp",EDGE,"E62"),sQuery(id+"F2.wireOp",EDGE,"E63")])]});
            deleteBodies(context, id + "F11", {"entities" : qUnion([Q0])});
        }
        {
            var Q0;
            Q0 = qSketchRegion(id + "F1", true);
            extrude(context, id + "F12", {"entities" : qUnion([Q0]), "depth" : 16 * mm});
        }
        {
            var Q0;
            Q0=makeQuery(id+"F12.opExtrude","SWEPT_BODY",BODY,{"disambiguationData":[OSD([sQuery(id+"F1.wireOp",EDGE,"E17.0"),sQuery(id+"F1.wireOp",EDGE,"E18.0"),sQuery(id+"F1.wireOp",EDGE,"E19.0"),sQuery(id+"F1.wireOp",EDGE,"E20.0"),sQuery(id+"F1.wireOp",EDGE,"E21.0"),sQuery(id+"F1.wireOp",EDGE,"E22.0"),sQuery(id+"F1.wireOp",EDGE,"E23.0"),sQuery(id+"F1.wireOp",EDGE,"E24.0"),sQuery(id+"F1.wireOp",EDGE,"E25.0"),sQuery(id+"F1.wireOp",EDGE,"E26.0"),sQuery(id+"F1.wireOp",EDGE,"E27.0"),sQuery(id+"F1.wireOp",EDGE,"E29.0"),sQuery(id+"F1.wireOp",EDGE,"E29.1"),sQuery(id+"F1.wireOp",EDGE,"E29.2"),sQuery(id+"F1.wireOp",EDGE,"E29.3"),sQuery(id+"F1.wireOp",EDGE,"E29.4"),sQuery(id+"F1.wireOp",EDGE,"E29.5"),sQuery(id+"F1.wireOp",EDGE,"E29.6"),sQuery(id+"F1.wireOp",EDGE,"E29.7"),sQuery(id+"F1.wireOp",EDGE,"E29.8"),sQuery(id+"F1.wireOp",EDGE,"E29.9"),sQuery(id+"F1.wireOp",EDGE,"E29.10"),sQuery(id+"F1.wireOp",EDGE,"E29.11"),sQuery(id+"F1.wireOp",EDGE,"E29.12"),sQuery(id+"F1.wireOp",EDGE,"E30.0"),sQuery(id+"F1.wireOp",EDGE,"E31"),sQuery(id+"F1.wireOp",EDGE,"E32"),sQuery(id+"F1.wireOp",EDGE,"E33"),sQuery(id+"F1.wireOp",EDGE,"E34.0"),sQuery(id+"F1.wireOp",EDGE,"E38.0"),sQuery(id+"F1.wireOp",EDGE,"E39"),sQuery(id+"F1.wireOp",EDGE,"E40")])]});
            var Q1;
            Q1=makeQuery(id+"F12.opExtrude","CAP_FACE",FACE,{"disambiguationData":[OSD([sQuery(id+"F1.wireOp",EDGE,"E17.0"),sQuery(id+"F1.wireOp",EDGE,"E18.0"),sQuery(id+"F1.wireOp",EDGE,"E19.0"),sQuery(id+"F1.wireOp",EDGE,"E20.0"),sQuery(id+"F1.wireOp",EDGE,"E21.0"),sQuery(id+"F1.wireOp",EDGE,"E22.0"),sQuery(id+"F1.wireOp",EDGE,"E23.0"),sQuery(id+"F1.wireOp",EDGE,"E24.0"),sQuery(id+"F1.wireOp",EDGE,"E25.0"),sQuery(id+"F1.wireOp",EDGE,"E26.0"),sQuery(id+"F1.wireOp",EDGE,"E27.0"),sQuery(id+"F1.wireOp",EDGE,"E29.0"),sQuery(id+"F1.wireOp",EDGE,"E29.1"),sQuery(id+"F1.wireOp",EDGE,"E29.2"),sQuery(id+"F1.wireOp",EDGE,"E29.3"),sQuery(id+"F1.wireOp",EDGE,"E29.4"),sQuery(id+"F1.wireOp",EDGE,"E29.5"),sQuery(id+"F1.wireOp",EDGE,"E29.6"),sQuery(id+"F1.wireOp",EDGE,"E29.7"),sQuery(id+"F1.wireOp",EDGE,"E29.8"),sQuery(id+"F1.wireOp",EDGE,"E29.9"),sQuery(id+"F1.wireOp",EDGE,"E29.10"),sQuery(id+"F1.wireOp",EDGE,"E29.11"),sQuery(id+"F1.wireOp",EDGE,"E29.12"),sQuery(id+"F1.wireOp",EDGE,"E30.0"),sQuery(id+"F1.wireOp",EDGE,"E31"),sQuery(id+"F1.wireOp",EDGE,"E32"),sQuery(id+"F1.wireOp",EDGE,"E33"),sQuery(id+"F1.wireOp",EDGE,"E34.0"),sQuery(id+"F1.wireOp",EDGE,"E38.0"),sQuery(id+"F1.wireOp",EDGE,"E39"),sQuery(id+"F1.wireOp",EDGE,"E40")])],"isStart":false});
            transform(context, id + "F13", {"entities" : qUnion([Q0]), "transformType" : TransformType.TRANSLATION_DISTANCE, "transformDirection" : qUnion([Q1]), "distance" : 8.5 * mm, "makeCopy" : false});
        }
        {
            var Q0;
            Q0 = qSketchRegion(id + "F8", true);
            extrude(context, id + "F14", {"entities" : qUnion([Q0]), "depth" : 3 * mm});
        }
        {
            var Q0;
            Q0 = qSketchRegion(id + "F4", true);
            extrude(context, id + "F15", {"entities" : qUnion([Q0]), "operationType" : NewBodyOperationType.ADD, "depth" : 5 * mm});
        }
        {
            var Q0;
            Q0 = qSketchRegion(id + "F6", true);
            extrude(context, id + "F16", {"entities" : qUnion([Q0]), "operationType" : NewBodyOperationType.ADD, "depth" : 0.5 * mm});
        }
        {
            var Q0;
            Q0=makeQuery(id+"F10.opPattern","COPY",EDGE,{"derivedFrom":makeQuery(id+"F3.opExtrude","CAP_EDGE",EDGE,{"disambiguationData":[OSD([sQuery(id+"F2.wireOp",EDGE,"E55.1"),sQuery(id+"F2.wireOp",EDGE,"E56")])],"isStart":false}),"instanceName":"1"});
            var Q1;
            Q1=makeQuery(id+"F10.opPattern","COPY",EDGE,{"derivedFrom":makeQuery(id+"F3.opExtrude","CAP_EDGE",EDGE,{"disambiguationData":[OSD([sQuery(id+"F2.wireOp",EDGE,"E55.1"),sQuery(id+"F2.wireOp",EDGE,"E56")])],"isStart":true}),"instanceName":"1"});
            var Q2;
            Q2=makeQuery(id+"F14.opExtrude","CAP_EDGE",EDGE,{"disambiguationData":[OSD([sQuery(id+"F8.wireOp",EDGE,"E126.0.4"),sQuery(id+"F8.wireOp",EDGE,"E126.0.5")])],"isStart":true});
            var Q3;
            Q3=makeQuery(id+"F14.opExtrude","CAP_EDGE",EDGE,{"disambiguationData":[OSD([sQuery(id+"F8.wireOp",EDGE,"E126.0.4"),sQuery(id+"F8.wireOp",EDGE,"E126.0.5")])],"isStart":false});
            fillet(context, id + "F17", {"entities" : qUnion([Q0, Q1, Q2, Q3]), "radius" : 1 * mm, "tangentPropagation" : true, "allowEdgeOverflow" : false});
        }
        {
            var Q0;
            Q0=makeQuery(id+"F12.opExtrude","CAP_EDGE",EDGE,{"disambiguationData":[OSD([sQuery(id+"F1.wireOp",EDGE,"E38.0")])],"isStart":true});
            var Q1;
            Q1=makeQuery(id+"F12.opExtrude","CAP_EDGE",EDGE,{"disambiguationData":[OSD([sQuery(id+"F1.wireOp",EDGE,"E38.0")])],"isStart":false});
            var Q2;
            Q2=makeQuery(id+"F12.opExtrude","SWEPT_EDGE",EDGE,{"disambiguationData":[OSD([sQuery(id+"F1.wireOp",EDGE,"E38.0"),sQuery(id+"F1.wireOp",EDGE,"E39")])]});
            var Q3;
            Q3=makeQuery(id+"F12.opExtrude","SWEPT_EDGE",EDGE,{"disambiguationData":[OSD([sQuery(id+"F1.wireOp",EDGE,"E38.0"),sQuery(id+"F1.wireOp",EDGE,"E40")])]});
            chamfer(context, id + "F18", {"entities" : qUnion([Q0, Q1, Q2, Q3]), "chamferType" : ChamferType.TWO_OFFSETS, "width1" : 1 * mm, "oppositeDirection" : false, "width2" : 2 * mm, "tangentPropagation" : true});
        }
        {
            var Q0;
            Q0=makeQuery(id+"F0.imprint","IMPRINT",FACE,{"disambiguationData":[TD([[makeQuery(id+"F0.imprint","IMPRINT",EDGE,{"derivedFrom":sQuery(id+"F0.wireOp",EDGE,"E0")}),1.0]])]});
            var sketch = newSketch(context, id + "F19", { "sketchPlane" : qUnion([Q0])});
            skLineSegment(sketch, "E130.0", {"start": v(-16.02, -9.14) * mm, "end": v(-7.63, -6.28) * mm});
            skArc(sketch, "E131.0", {"start": v(-5.04, -5.85) * mm, "mid": v(-6.35, -5.96) * mm, "end": v(-7.63, -6.28) * mm});
            skLineSegment(sketch, "E132.0", {"start": v(-5.04, -5.85) * mm, "end": v(0, -5.85) * mm});
            skLineSegment(sketch, "E133.0", {"start": v(0, -5.85) * mm, "end": v(5.04, -5.85) * mm});
            skArc(sketch, "E134.0", {"start": v(12.12, -10.12) * mm, "mid": v(9.18, -7) * mm, "end": v(5.04, -5.85) * mm});
            skCircle(sketch, "E135.0", {"center": v(-14.73, -12.93) * mm, "radius": 2 * mm});
            skArc(sketch, "E136.0", {"start": v(-16.02, -9.14) * mm, "mid": v(-16.46, -9.32) * mm, "end": v(-16.86, -9.54) * mm});
            skArc(sketch, "E137", {"start": v(-16.86, -9.54) * mm, "mid": v(-18.27, -15.75) * mm, "end": v(-12.07, -17.16) * mm});
            skLineSegment(sketch, "E138.0", {"start": v(-8.54, -16.2) * mm, "end": v(-18.32, -11.03) * mm, "construction": true});
            skArc(sketch, "E139.0", {"start": v(-5.04, -9.85) * mm, "mid": v(-7.1, -10.42) * mm, "end": v(-8.58, -11.98) * mm, "construction": true});
            skLineSegment(sketch, "E140.0", {"start": v(-5.04, -9.85) * mm, "end": v(0, -9.85) * mm, "construction": true});
            skLineSegment(sketch, "E141.0", {"start": v(0, -9.85) * mm, "end": v(5.04, -9.85) * mm, "construction": true});
            skArc(sketch, "E142.0", {"start": v(8.58, -11.98) * mm, "mid": v(7.1, -10.42) * mm, "end": v(5.04, -9.85) * mm, "construction": true});
            skArc(sketch, "E143.0", {"start": v(-5.04, -9.35) * mm, "mid": v(-7.55, -10.11) * mm, "end": v(-9.2, -12.14) * mm});
            skLineSegment(sketch, "E143.1", {"start": v(-5.04, -9.35) * mm, "end": v(0, -9.35) * mm});
            skLineSegment(sketch, "E143.2", {"start": v(0, -9.35) * mm, "end": v(5.04, -9.35) * mm});
            skArc(sketch, "E143.3", {"start": v(9.03, -11.76) * mm, "mid": v(7.37, -10) * mm, "end": v(5.04, -9.35) * mm});
            skArc(sketch, "E144", {"start": v(12.12, -10.12) * mm, "mid": v(12.4, -10.45) * mm, "end": v(12.8, -10.63) * mm});
            skArc(sketch, "E145", {"start": v(9.02, -11.75) * mm, "mid": v(10.28, -13.24) * mm, "end": v(12.05, -14.05) * mm});
            skLineSegment(sketch, "E146", {"start": v(5.04, -13.85) * mm, "end": v(8.58, -11.98) * mm, "construction": true});
            skLineSegment(sketch, "E147", {"start": v(8.58, -11.98) * mm, "end": v(13, -9.65) * mm, "construction": true});
            skLineSegment(sketch, "E148", {"start": v(13, -9.65) * mm, "end": v(11.23, -17.88) * mm, "construction": true});
            skPoint(sketch, "E149.orphan", {"position": v(12.32, -10.52) * mm});
            skLineSegment(sketch, "E150", {"start": v(12.8, -10.63) * mm, "end": v(15.73, -11.26) * mm});
            skLineSegment(sketch, "E151", {"start": v(12.05, -14.05) * mm, "end": v(14.99, -14.68) * mm});
            skLineSegment(sketch, "E152", {"start": v(14.99, -14.68) * mm, "end": v(15.73, -11.26) * mm});
            skLineSegment(sketch, "E153", {"start": v(-16.86, -9.54) * mm, "end": v(-12.07, -17.16) * mm, "construction": true});
            skArc(sketch, "E154", {"start": v(-12.07, -17.16) * mm, "mid": v(-11.1, -16.3) * mm, "end": v(-10.46, -15.18) * mm});
            skLineSegment(sketch, "E155", {"start": v(-9.2, -12.14) * mm, "end": v(-10.45, -15.18) * mm});
            skSolve(sketch);
        }
        {
            var Q0;
            Q0=makeQuery(id+"F0.imprint","IMPRINT",FACE,{"disambiguationData":[TD([[makeQuery(id+"F0.imprint","IMPRINT",EDGE,{"derivedFrom":sQuery(id+"F0.wireOp",EDGE,"E0")}),1.0]])]});
            var sketch = newSketch(context, id + "F20", { "sketchPlane" : qUnion([Q0])});
            skCircle(sketch, "E156.0", {"center": v(-14.73, -12.93) * mm, "radius": 2 * mm});
            skArc(sketch, "E157.0", {"start": v(-16.02, -9.14) * mm, "mid": v(-16.46, -9.32) * mm, "end": v(-16.86, -9.54) * mm});
            skLineSegment(sketch, "E158.0", {"start": v(-16.02, -9.14) * mm, "end": v(-7.63, -6.28) * mm});
            skArc(sketch, "E159.0", {"start": v(-5.04, -5.85) * mm, "mid": v(-6.35, -5.96) * mm, "end": v(-7.63, -6.28) * mm});
            skLineSegment(sketch, "E160.0", {"start": v(-5.04, -5.85) * mm, "end": v(0, -5.85) * mm});
            skLineSegment(sketch, "E161.0", {"start": v(0, -5.85) * mm, "end": v(5.04, -5.85) * mm});
            skArc(sketch, "E162.0", {"start": v(12.32, -10.52) * mm, "mid": v(9.37, -7.12) * mm, "end": v(5.04, -5.85) * mm});
            skLineSegment(sketch, "E163", {"start": v(-16.86, -9.54) * mm, "end": v(-11.05, -18.77) * mm, "construction": true});
            skPoint(sketch, "E164.orphan", {"position": v(-17.37, -15.94) * mm});
            skArc(sketch, "E165", {"start": v(-16.86, -9.54) * mm, "mid": v(-18.35, -16.1) * mm, "end": v(-11.8, -17.58) * mm});
            skArc(sketch, "E166", {"start": v(-11.8, -17.58) * mm, "mid": v(-10.71, -16.57) * mm, "end": v(-10.07, -15.23) * mm});
            skLineSegment(sketch, "E167", {"start": v(5.04, -13.85) * mm, "end": v(16.35, -8.68) * mm, "construction": true});
            skLineSegment(sketch, "E168", {"start": v(14.14, -9.69) * mm, "end": v(11.75, -18.34) * mm, "construction": true});
            skArc(sketch, "E169", {"start": v(12.32, -10.52) * mm, "mid": v(12.84, -11.21) * mm, "end": v(13.6, -11.62) * mm});
            skLineSegment(sketch, "E170", {"start": v(13.6, -11.62) * mm, "end": v(16.5, -12.42) * mm});
            skArc(sketch, "E171.0", {"start": v(-5.04, -9.35) * mm, "mid": v(-7.79, -10.28) * mm, "end": v(-9.4, -12.69) * mm});
            skLineSegment(sketch, "E171.1", {"start": v(-5.04, -9.35) * mm, "end": v(0, -9.35) * mm});
            skLineSegment(sketch, "E171.2", {"start": v(12.68, -15) * mm, "end": v(15.57, -15.79) * mm});
            skArc(sketch, "E171.3", {"start": v(9.14, -11.98) * mm, "mid": v(10.57, -13.88) * mm, "end": v(12.68, -15) * mm});
            skArc(sketch, "E171.4", {"start": v(9.14, -11.98) * mm, "mid": v(7.48, -10.06) * mm, "end": v(5.04, -9.35) * mm});
            skLineSegment(sketch, "E171.5", {"start": v(0, -9.35) * mm, "end": v(5.04, -9.35) * mm});
            skLineSegment(sketch, "E172", {"start": v(-9.4, -12.69) * mm, "end": v(-10.07, -15.23) * mm});
            skLineSegment(sketch, "E173", {"start": v(15.57, -15.79) * mm, "end": v(16.5, -12.42) * mm});
            skCircle(sketch, "E174", {"center": v(-14.73, -12.93) * mm, "radius": 4 * mm, "construction": true});
            skCircle(sketch, "E175", {"center": v(-5.04, -5.85) * mm, "radius": 0.75 * mm});
            skCircle(sketch, "E176.1.0.0", {"center": v(-2.04, -5.85) * mm, "radius": 0.75 * mm});
            skCircle(sketch, "E176.2.0.0", {"center": v(0.96, -5.85) * mm, "radius": 0.75 * mm});
            skCircle(sketch, "E176.3.0.0", {"center": v(3.96, -5.85) * mm, "radius": 0.75 * mm});
            skLineSegment(sketch, "E176.direction1", {"start": v(-5.04, -5.85) * mm, "end": v(-2.04, -5.85) * mm, "construction": true});
            skCircle(sketch, "E177", {"center": v(6.96, -6.08) * mm, "radius": 0.75 * mm});
            skCircle(sketch, "E178", {"center": v(9.68, -7.33) * mm, "radius": 0.75 * mm});
            skCircle(sketch, "E179", {"center": v(11.76, -9.5) * mm, "radius": 0.75 * mm});
            skCircle(sketch, "E180", {"center": v(-8, -6.4) * mm, "radius": 0.75 * mm});
            skSolve(sketch);
        }
        {
            var Q0;
            Q0 = qSketchRegion(id + "F20", true);
            extrude(context, id + "F21", {"entities" : qUnion([Q0]), "depth" : 16 * mm});
        }
        {
            var Q0;
            Q0=makeQuery(id+"F21.opExtrude","SWEPT_BODY",BODY,{"disambiguationData":[OSD([sQuery(id+"F20.wireOp",EDGE,"E156.0"),sQuery(id+"F20.wireOp",EDGE,"E157.0"),sQuery(id+"F20.wireOp",EDGE,"E158.0"),sQuery(id+"F20.wireOp",EDGE,"E159.0"),sQuery(id+"F20.wireOp",EDGE,"E160.0"),sQuery(id+"F20.wireOp",EDGE,"E161.0"),sQuery(id+"F20.wireOp",EDGE,"E162.0"),sQuery(id+"F20.wireOp",EDGE,"E165"),sQuery(id+"F20.wireOp",EDGE,"E166"),sQuery(id+"F20.wireOp",EDGE,"E169"),sQuery(id+"F20.wireOp",EDGE,"E170"),sQuery(id+"F20.wireOp",EDGE,"E171.0"),sQuery(id+"F20.wireOp",EDGE,"E171.1"),sQuery(id+"F20.wireOp",EDGE,"E171.2"),sQuery(id+"F20.wireOp",EDGE,"E171.3"),sQuery(id+"F20.wireOp",EDGE,"E171.4"),sQuery(id+"F20.wireOp",EDGE,"E171.5"),sQuery(id+"F20.wireOp",EDGE,"E172"),sQuery(id+"F20.wireOp",EDGE,"E173")])]});
            var Q1;
            Q1=makeQuery(id+"F21.opExtrude","CAP_FACE",FACE,{"disambiguationData":[OSD([sQuery(id+"F20.wireOp",EDGE,"E156.0"),sQuery(id+"F20.wireOp",EDGE,"E157.0"),sQuery(id+"F20.wireOp",EDGE,"E158.0"),sQuery(id+"F20.wireOp",EDGE,"E159.0"),sQuery(id+"F20.wireOp",EDGE,"E160.0"),sQuery(id+"F20.wireOp",EDGE,"E161.0"),sQuery(id+"F20.wireOp",EDGE,"E162.0"),sQuery(id+"F20.wireOp",EDGE,"E165"),sQuery(id+"F20.wireOp",EDGE,"E166"),sQuery(id+"F20.wireOp",EDGE,"E169"),sQuery(id+"F20.wireOp",EDGE,"E170"),sQuery(id+"F20.wireOp",EDGE,"E171.0"),sQuery(id+"F20.wireOp",EDGE,"E171.1"),sQuery(id+"F20.wireOp",EDGE,"E171.2"),sQuery(id+"F20.wireOp",EDGE,"E171.3"),sQuery(id+"F20.wireOp",EDGE,"E171.4"),sQuery(id+"F20.wireOp",EDGE,"E171.5"),sQuery(id+"F20.wireOp",EDGE,"E172"),sQuery(id+"F20.wireOp",EDGE,"E173")])],"isStart":false});
            transform(context, id + "F22", {"entities" : qUnion([Q0]), "transformType" : TransformType.TRANSLATION_DISTANCE, "transformDirection" : qUnion([Q1]), "distance" : 8.5 * mm, "makeCopy" : false});
        }
        {
            var Q0;
            Q0=makeQuery(id+"F0.imprint","IMPRINT",FACE,{"disambiguationData":[TD([[makeQuery(id+"F0.imprint","IMPRINT",EDGE,{"derivedFrom":sQuery(id+"F0.wireOp",EDGE,"E0")}),1.0]])]});
            var sketch = newSketch(context, id + "F23", { "sketchPlane" : qUnion([Q0])});
            skLineSegment(sketch, "E181.0", {"start": v(-16.02, -9.14) * mm, "end": v(-10.82, -7.37) * mm, "construction": true});
            skArc(sketch, "E182.0", {"start": v(-5.04, -5.85) * mm, "mid": v(-6.35, -5.96) * mm, "end": v(-7.63, -6.28) * mm});
            skLineSegment(sketch, "E183.0", {"start": v(-5.04, -5.85) * mm, "end": v(0, -5.85) * mm});
            skLineSegment(sketch, "E184.0", {"start": v(0, -5.85) * mm, "end": v(5.04, -5.85) * mm});
            skArc(sketch, "E185.0", {"start": v(12.12, -10.12) * mm, "mid": v(9.18, -7) * mm, "end": v(5.04, -5.85) * mm});
            skArc(sketch, "E186.0", {"start": v(12.12, -10.12) * mm, "mid": v(12.4, -10.45) * mm, "end": v(12.8, -10.63) * mm});
            skLineSegment(sketch, "E187.0", {"start": v(12.8, -10.63) * mm, "end": v(15.73, -11.26) * mm});
            skLineSegment(sketch, "E188.0", {"start": v(14.99, -14.68) * mm, "end": v(15.73, -11.26) * mm});
            skLineSegment(sketch, "E189.0", {"start": v(12.05, -14.05) * mm, "end": v(14.99, -14.68) * mm});
            skArc(sketch, "E190.0", {"start": v(9.02, -11.75) * mm, "mid": v(10.28, -13.24) * mm, "end": v(12.05, -14.05) * mm});
            skArc(sketch, "E191.0", {"start": v(9.03, -11.76) * mm, "mid": v(7.37, -10) * mm, "end": v(5.04, -9.35) * mm});
            skLineSegment(sketch, "E192.0", {"start": v(0, -9.35) * mm, "end": v(5.04, -9.35) * mm});
            skLineSegment(sketch, "E193.0", {"start": v(-5.04, -9.35) * mm, "end": v(0, -9.35) * mm});
            skArc(sketch, "E194.0", {"start": v(-16.02, -9.14) * mm, "mid": v(-18.66, -12.15) * mm, "end": v(-17.37, -15.94) * mm, "construction": true});
            skArc(sketch, "E195.0", {"start": v(-17.37, -15.94) * mm, "mid": v(-11.72, -15.56) * mm, "end": v(-12.1, -9.92) * mm, "construction": true});
            skArc(sketch, "E196.0", {"start": v(-12.1, -9.92) * mm, "mid": v(-13.96, -9) * mm, "end": v(-16.02, -9.14) * mm, "construction": true});
            skLineSegment(sketch, "E197", {"start": v(-9.69, -10.68) * mm, "end": v(-10.82, -7.37) * mm});
            skLineSegment(sketch, "E198", {"start": v(-10.82, -7.37) * mm, "end": v(-7.63, -6.28) * mm});
            skArc(sketch, "E199.0", {"start": v(-5.04, -9.35) * mm, "mid": v(-5.78, -9.4) * mm, "end": v(-6.5, -9.6) * mm});
            skLineSegment(sketch, "E199.1", {"start": v(-9.69, -10.68) * mm, "end": v(-6.5, -9.6) * mm});
            skSolve(sketch);
        }
        {
            var Q0;
            Q0=makeQuery(id+"F0.imprint","IMPRINT",FACE,{"disambiguationData":[TD([[makeQuery(id+"F0.imprint","IMPRINT",EDGE,{"derivedFrom":sQuery(id+"F0.wireOp",EDGE,"E0")}),1.0]])]});
            var sketch = newSketch(context, id + "F24", { "sketchPlane" : qUnion([Q0])});
            skLineSegment(sketch, "E200.0", {"start": v(12.68, -15) * mm, "end": v(15.57, -15.79) * mm});
            skArc(sketch, "E201.0", {"start": v(9.14, -11.98) * mm, "mid": v(10.57, -13.88) * mm, "end": v(12.68, -15) * mm});
            skArc(sketch, "E202.0", {"start": v(9.14, -11.98) * mm, "mid": v(7.48, -10.06) * mm, "end": v(5.04, -9.35) * mm});
            skLineSegment(sketch, "E203.0", {"start": v(0, -9.35) * mm, "end": v(5.04, -9.35) * mm});
            skLineSegment(sketch, "E204.0", {"start": v(-5.04, -9.35) * mm, "end": v(0, -9.35) * mm});
            skArc(sketch, "E205.0", {"start": v(-5.04, -5.85) * mm, "mid": v(-6.35, -5.96) * mm, "end": v(-7.63, -6.28) * mm});
            skLineSegment(sketch, "E206.0", {"start": v(-5.04, -5.85) * mm, "end": v(0, -5.85) * mm});
            skLineSegment(sketch, "E207.0", {"start": v(0, -5.85) * mm, "end": v(5.04, -5.85) * mm});
            skArc(sketch, "E208.0", {"start": v(12.32, -10.52) * mm, "mid": v(9.37, -7.12) * mm, "end": v(5.04, -5.85) * mm});
            skArc(sketch, "E209.0", {"start": v(12.32, -10.52) * mm, "mid": v(12.84, -11.21) * mm, "end": v(13.6, -11.62) * mm});
            skLineSegment(sketch, "E210.0", {"start": v(13.6, -11.62) * mm, "end": v(16.5, -12.42) * mm});
            skLineSegment(sketch, "E211.0", {"start": v(15.57, -15.79) * mm, "end": v(16.5, -12.42) * mm});
            skLineSegment(sketch, "E212", {"start": v(-7.63, -6.28) * mm, "end": v(-10.82, -7.37) * mm});
            skLineSegment(sketch, "E213", {"start": v(-10.82, -7.37) * mm, "end": v(-9.69, -10.68) * mm});
            skArc(sketch, "E214", {"start": v(-5.04, -9.35) * mm, "mid": v(-5.78, -9.4) * mm, "end": v(-6.5, -9.6) * mm});
            skLineSegment(sketch, "E215", {"start": v(-9.69, -10.68) * mm, "end": v(-6.5, -9.6) * mm});
            skSolve(sketch);
        }
        {
            var Q0;
            Q0 = qSketchRegion(id + "F24", true);
            extrude(context, id + "F25", {"entities" : qUnion([Q0]), "depth" : 4.5 * mm});
        }
        {
            var Q0;
            Q0=makeQuery(id+"F25.opExtrude","SWEPT_BODY",BODY,{"disambiguationData":[OSD([sQuery(id+"F24.wireOp",EDGE,"E200.0"),sQuery(id+"F24.wireOp",EDGE,"E201.0"),sQuery(id+"F24.wireOp",EDGE,"E202.0"),sQuery(id+"F24.wireOp",EDGE,"E203.0"),sQuery(id+"F24.wireOp",EDGE,"E204.0"),sQuery(id+"F24.wireOp",EDGE,"E205.0"),sQuery(id+"F24.wireOp",EDGE,"E206.0"),sQuery(id+"F24.wireOp",EDGE,"E207.0"),sQuery(id+"F24.wireOp",EDGE,"E208.0"),sQuery(id+"F24.wireOp",EDGE,"E209.0"),sQuery(id+"F24.wireOp",EDGE,"E210.0"),sQuery(id+"F24.wireOp",EDGE,"E211.0"),sQuery(id+"F24.wireOp",EDGE,"E212"),sQuery(id+"F24.wireOp",EDGE,"E213"),sQuery(id+"F24.wireOp",EDGE,"E214"),sQuery(id+"F24.wireOp",EDGE,"E215")])]});
            var Q1;
            Q1=makeQuery(id+"F25.opExtrude","CAP_FACE",FACE,{"disambiguationData":[OSD([sQuery(id+"F24.wireOp",EDGE,"E200.0"),sQuery(id+"F24.wireOp",EDGE,"E201.0"),sQuery(id+"F24.wireOp",EDGE,"E202.0"),sQuery(id+"F24.wireOp",EDGE,"E203.0"),sQuery(id+"F24.wireOp",EDGE,"E204.0"),sQuery(id+"F24.wireOp",EDGE,"E205.0"),sQuery(id+"F24.wireOp",EDGE,"E206.0"),sQuery(id+"F24.wireOp",EDGE,"E207.0"),sQuery(id+"F24.wireOp",EDGE,"E208.0"),sQuery(id+"F24.wireOp",EDGE,"E209.0"),sQuery(id+"F24.wireOp",EDGE,"E210.0"),sQuery(id+"F24.wireOp",EDGE,"E211.0"),sQuery(id+"F24.wireOp",EDGE,"E212"),sQuery(id+"F24.wireOp",EDGE,"E213"),sQuery(id+"F24.wireOp",EDGE,"E214"),sQuery(id+"F24.wireOp",EDGE,"E215")])],"isStart":false});
            transform(context, id + "F26", {"entities" : qUnion([Q0]), "transformType" : TransformType.TRANSLATION_DISTANCE, "transformDirection" : qUnion([Q1]), "distance" : 4 * mm, "makeCopy" : false});
        }
        {
            var Q0;
            Q0 = qSketchRegion(id + "F24", true);
            extrude(context, id + "F27", {"entities" : qUnion([Q0]), "depth" : 4.5 * mm});
        }
        {
            var Q0;
            Q0=makeQuery(id+"F27.opExtrude","SWEPT_BODY",BODY,{"disambiguationData":[OSD([sQuery(id+"F24.wireOp",EDGE,"E200.0"),sQuery(id+"F24.wireOp",EDGE,"E201.0"),sQuery(id+"F24.wireOp",EDGE,"E202.0"),sQuery(id+"F24.wireOp",EDGE,"E203.0"),sQuery(id+"F24.wireOp",EDGE,"E204.0"),sQuery(id+"F24.wireOp",EDGE,"E205.0"),sQuery(id+"F24.wireOp",EDGE,"E206.0"),sQuery(id+"F24.wireOp",EDGE,"E207.0"),sQuery(id+"F24.wireOp",EDGE,"E208.0"),sQuery(id+"F24.wireOp",EDGE,"E209.0"),sQuery(id+"F24.wireOp",EDGE,"E210.0"),sQuery(id+"F24.wireOp",EDGE,"E211.0"),sQuery(id+"F24.wireOp",EDGE,"E212"),sQuery(id+"F24.wireOp",EDGE,"E213"),sQuery(id+"F24.wireOp",EDGE,"E214"),sQuery(id+"F24.wireOp",EDGE,"E215")])]});
            var Q1;
            Q1=makeQuery(id+"F27.opExtrude","CAP_FACE",FACE,{"disambiguationData":[OSD([sQuery(id+"F24.wireOp",EDGE,"E200.0"),sQuery(id+"F24.wireOp",EDGE,"E201.0"),sQuery(id+"F24.wireOp",EDGE,"E202.0"),sQuery(id+"F24.wireOp",EDGE,"E203.0"),sQuery(id+"F24.wireOp",EDGE,"E204.0"),sQuery(id+"F24.wireOp",EDGE,"E205.0"),sQuery(id+"F24.wireOp",EDGE,"E206.0"),sQuery(id+"F24.wireOp",EDGE,"E207.0"),sQuery(id+"F24.wireOp",EDGE,"E208.0"),sQuery(id+"F24.wireOp",EDGE,"E209.0"),sQuery(id+"F24.wireOp",EDGE,"E210.0"),sQuery(id+"F24.wireOp",EDGE,"E211.0"),sQuery(id+"F24.wireOp",EDGE,"E212"),sQuery(id+"F24.wireOp",EDGE,"E213"),sQuery(id+"F24.wireOp",EDGE,"E214"),sQuery(id+"F24.wireOp",EDGE,"E215")])],"isStart":false});
            transform(context, id + "F28", {"entities" : qUnion([Q0]), "transformType" : TransformType.TRANSLATION_DISTANCE, "transformDirection" : qUnion([Q1]), "distance" : 24.5 * mm, "makeCopy" : false});
        }
        {
            var Q0;
            Q0=makeQuery(id+"F25.opExtrude","SWEPT_BODY",BODY,{"disambiguationData":[OSD([sQuery(id+"F24.wireOp",EDGE,"E200.0"),sQuery(id+"F24.wireOp",EDGE,"E201.0"),sQuery(id+"F24.wireOp",EDGE,"E202.0"),sQuery(id+"F24.wireOp",EDGE,"E203.0"),sQuery(id+"F24.wireOp",EDGE,"E204.0"),sQuery(id+"F24.wireOp",EDGE,"E205.0"),sQuery(id+"F24.wireOp",EDGE,"E206.0"),sQuery(id+"F24.wireOp",EDGE,"E207.0"),sQuery(id+"F24.wireOp",EDGE,"E208.0"),sQuery(id+"F24.wireOp",EDGE,"E209.0"),sQuery(id+"F24.wireOp",EDGE,"E210.0"),sQuery(id+"F24.wireOp",EDGE,"E211.0"),sQuery(id+"F24.wireOp",EDGE,"E212"),sQuery(id+"F24.wireOp",EDGE,"E213"),sQuery(id+"F24.wireOp",EDGE,"E214"),sQuery(id+"F24.wireOp",EDGE,"E215")])]});
            var Q1;
            Q1=makeQuery(id+"F21.opExtrude","SWEPT_BODY",BODY,{"disambiguationData":[OSD([sQuery(id+"F20.wireOp",EDGE,"E156.0"),sQuery(id+"F20.wireOp",EDGE,"E157.0"),sQuery(id+"F20.wireOp",EDGE,"E158.0"),sQuery(id+"F20.wireOp",EDGE,"E159.0"),sQuery(id+"F20.wireOp",EDGE,"E160.0"),sQuery(id+"F20.wireOp",EDGE,"E161.0"),sQuery(id+"F20.wireOp",EDGE,"E162.0"),sQuery(id+"F20.wireOp",EDGE,"E165"),sQuery(id+"F20.wireOp",EDGE,"E166"),sQuery(id+"F20.wireOp",EDGE,"E169"),sQuery(id+"F20.wireOp",EDGE,"E170"),sQuery(id+"F20.wireOp",EDGE,"E171.0"),sQuery(id+"F20.wireOp",EDGE,"E171.1"),sQuery(id+"F20.wireOp",EDGE,"E171.2"),sQuery(id+"F20.wireOp",EDGE,"E171.3"),sQuery(id+"F20.wireOp",EDGE,"E171.4"),sQuery(id+"F20.wireOp",EDGE,"E171.5"),sQuery(id+"F20.wireOp",EDGE,"E172"),sQuery(id+"F20.wireOp",EDGE,"E173")])]});
            var Q2;
            Q2=makeQuery(id+"F27.opExtrude","SWEPT_BODY",BODY,{"disambiguationData":[OSD([sQuery(id+"F24.wireOp",EDGE,"E200.0"),sQuery(id+"F24.wireOp",EDGE,"E201.0"),sQuery(id+"F24.wireOp",EDGE,"E202.0"),sQuery(id+"F24.wireOp",EDGE,"E203.0"),sQuery(id+"F24.wireOp",EDGE,"E204.0"),sQuery(id+"F24.wireOp",EDGE,"E205.0"),sQuery(id+"F24.wireOp",EDGE,"E206.0"),sQuery(id+"F24.wireOp",EDGE,"E207.0"),sQuery(id+"F24.wireOp",EDGE,"E208.0"),sQuery(id+"F24.wireOp",EDGE,"E209.0"),sQuery(id+"F24.wireOp",EDGE,"E210.0"),sQuery(id+"F24.wireOp",EDGE,"E211.0"),sQuery(id+"F24.wireOp",EDGE,"E212"),sQuery(id+"F24.wireOp",EDGE,"E213"),sQuery(id+"F24.wireOp",EDGE,"E214"),sQuery(id+"F24.wireOp",EDGE,"E215")])]});
            booleanBodies(context, id + "F29", {"operationType" : BooleanOperationType.UNION, "tools" : qUnion([Q0, Q1, Q2])});
        }
        {
            var Q0;
            Q0=makeQuery(id+"F25.opExtrude","CAP_EDGE",EDGE,{"disambiguationData":[OSD([sQuery(id+"F24.wireOp",EDGE,"E211.0")])],"isStart":true});
            var Q1;
            Q1=makeQuery(id+"F25.opExtrude","CAP_EDGE",EDGE,{"disambiguationData":[OSD([sQuery(id+"F24.wireOp",EDGE,"E213")])],"isStart":true});
            var Q2;
            Q2=makeQuery(id+"F27.opExtrude","CAP_EDGE",EDGE,{"disambiguationData":[OSD([sQuery(id+"F24.wireOp",EDGE,"E213")])],"isStart":false});
            var Q3;
            Q3=makeQuery(id+"F27.opExtrude","CAP_EDGE",EDGE,{"disambiguationData":[OSD([sQuery(id+"F24.wireOp",EDGE,"E211.0")])],"isStart":false});
            fillet(context, id + "F30", {"entities" : qUnion([Q0, Q1, Q2, Q3]), "radius" : 3 * mm, "tangentPropagation" : true, "allowEdgeOverflow" : false});
        }
        {
            var Q0;
            {var subQ0=sQuery(id+"F23.wireOp",EDGE,"E198");Q0=makeQuery(id+"F30.opFillet","BLEND_EDGE",EDGE,{"blendedFrom":[makeQuery(id+"F25.opExtrude","CAP_EDGE",EDGE,{"disambiguationData":[OSD([sQuery(id+"F23.wireOp",EDGE,"E197")])],"isStart":true}),makeQuery(id+"F29.opBoolean","MERGE",FACE,{"derivedFrom":[makeQuery(id+"F21.opExtrude","SWEPT_FACE",FACE,{"disambiguationData":[OSD([sQuery(id+"F19.wireOp",EDGE,"E130.0")])]}),makeQuery(id+"F25.opExtrude","SWEPT_FACE",FACE,{"disambiguationData":[OSD([subQ0])]}),makeQuery(id+"F27.opExtrude","SWEPT_FACE",FACE,{"disambiguationData":[OSD([subQ0])]})]})],"blendedInto":[makeQuery(id+"F29.opBoolean","MERGE",FACE,{"derivedFrom":[makeQuery(id+"F21.opExtrude","SWEPT_FACE",FACE,{"disambiguationData":[OSD([sQuery(id+"F19.wireOp",EDGE,"E130.0")])]}),makeQuery(id+"F25.opExtrude","SWEPT_FACE",FACE,{"disambiguationData":[OSD([subQ0])]}),makeQuery(id+"F27.opExtrude","SWEPT_FACE",FACE,{"disambiguationData":[OSD([subQ0])]})]})]});}
            var Q1;
            Q1=makeQuery(id+"F30.opFillet","BLEND_EDGE",EDGE,{"blendedFrom":[makeQuery(id+"F25.opExtrude","CAP_EDGE",EDGE,{"disambiguationData":[OSD([sQuery(id+"F23.wireOp",EDGE,"E197")])],"isStart":true}),makeQuery(id+"F25.opExtrude","SWEPT_FACE",FACE,{"disambiguationData":[OSD([sQuery(id+"F23.wireOp",EDGE,"E199.1")])]})],"blendedInto":[makeQuery(id+"F25.opExtrude","SWEPT_FACE",FACE,{"disambiguationData":[OSD([sQuery(id+"F23.wireOp",EDGE,"E199.1")])]})]});
            var Q2;
            Q2=makeQuery(id+"F27.opExtrude","CAP_EDGE",EDGE,{"disambiguationData":[OSD([sQuery(id+"F24.wireOp",EDGE,"E206.0"),sQuery(id+"F24.wireOp",EDGE,"E207.0")])],"isStart":false});
            var Q3;
            Q3=makeQuery(id+"F27.opExtrude","CAP_EDGE",EDGE,{"disambiguationData":[OSD([sQuery(id+"F24.wireOp",EDGE,"E203.0"),sQuery(id+"F24.wireOp",EDGE,"E204.0")])],"isStart":false});
            fillet(context, id + "F31", {"entities" : qUnion([Q0, Q1, Q2, Q3]), "radius" : 1 * mm, "tangentPropagation" : true, "defaultsChanged" : false, "vertexSettings" : [], "allowEdgeOverflow" : false});
        }
        {
            var Q0;
            Q0=makeQuery(id+"F21.opExtrude","CAP_EDGE",EDGE,{"disambiguationData":[OSD([sQuery(id+"F20.wireOp",EDGE,"E175")])],"isStart":false});
            var Q1;
            Q1=makeQuery(id+"F21.opExtrude","CAP_EDGE",EDGE,{"disambiguationData":[OSD([sQuery(id+"F20.wireOp",EDGE,"E176.1.0.0")])],"isStart":false});
            var Q2;
            Q2=makeQuery(id+"F21.opExtrude","CAP_EDGE",EDGE,{"disambiguationData":[OSD([sQuery(id+"F20.wireOp",EDGE,"E176.2.0.0")])],"isStart":false});
            var Q3;
            Q3=makeQuery(id+"F21.opExtrude","CAP_EDGE",EDGE,{"disambiguationData":[OSD([sQuery(id+"F20.wireOp",EDGE,"E176.3.0.0")])],"isStart":false});
            var Q4;
            Q4=makeQuery(id+"F21.opExtrude","CAP_EDGE",EDGE,{"disambiguationData":[OSD([sQuery(id+"F20.wireOp",EDGE,"E177")])],"isStart":false});
            var Q5;
            Q5=makeQuery(id+"F21.opExtrude","CAP_EDGE",EDGE,{"disambiguationData":[OSD([sQuery(id+"F20.wireOp",EDGE,"E178")])],"isStart":false});
            var Q6;
            Q6=makeQuery(id+"F21.opExtrude","CAP_EDGE",EDGE,{"disambiguationData":[OSD([sQuery(id+"F20.wireOp",EDGE,"E179")])],"isStart":false});
            var Q7;
            Q7=makeQuery(id+"F21.opExtrude","CAP_EDGE",EDGE,{"disambiguationData":[OSD([sQuery(id+"F20.wireOp",EDGE,"E179")])],"isStart":true});
            var Q8;
            Q8=makeQuery(id+"F21.opExtrude","CAP_EDGE",EDGE,{"disambiguationData":[OSD([sQuery(id+"F20.wireOp",EDGE,"E178")])],"isStart":true});
            var Q9;
            Q9=makeQuery(id+"F21.opExtrude","CAP_EDGE",EDGE,{"disambiguationData":[OSD([sQuery(id+"F20.wireOp",EDGE,"E177")])],"isStart":true});
            var Q10;
            Q10=makeQuery(id+"F21.opExtrude","CAP_EDGE",EDGE,{"disambiguationData":[OSD([sQuery(id+"F20.wireOp",EDGE,"E176.3.0.0")])],"isStart":true});
            var Q11;
            Q11=makeQuery(id+"F21.opExtrude","CAP_EDGE",EDGE,{"disambiguationData":[OSD([sQuery(id+"F20.wireOp",EDGE,"E176.2.0.0")])],"isStart":true});
            var Q12;
            Q12=makeQuery(id+"F21.opExtrude","CAP_EDGE",EDGE,{"disambiguationData":[OSD([sQuery(id+"F20.wireOp",EDGE,"E176.1.0.0")])],"isStart":true});
            var Q13;
            Q13=makeQuery(id+"F21.opExtrude","CAP_EDGE",EDGE,{"disambiguationData":[OSD([sQuery(id+"F20.wireOp",EDGE,"E175")])],"isStart":true});
            var Q14;
            Q14=makeQuery(id+"F21.opExtrude","CAP_EDGE",EDGE,{"disambiguationData":[OSD([sQuery(id+"F20.wireOp",EDGE,"E180")])],"isStart":false});
            var Q15;
            Q15=makeQuery(id+"F21.opExtrude","CAP_EDGE",EDGE,{"disambiguationData":[OSD([sQuery(id+"F20.wireOp",EDGE,"E180")])],"isStart":true});
            fillet(context, id + "F32", {"entities" : qUnion([Q0, Q1, Q2, Q3, Q4, Q5, Q6, Q7, Q8, Q9, Q10, Q11, Q12, Q13, Q14, Q15]), "radius" : 0.75 * mm, "tangentPropagation" : true, "allowEdgeOverflow" : false});
        }
    });
